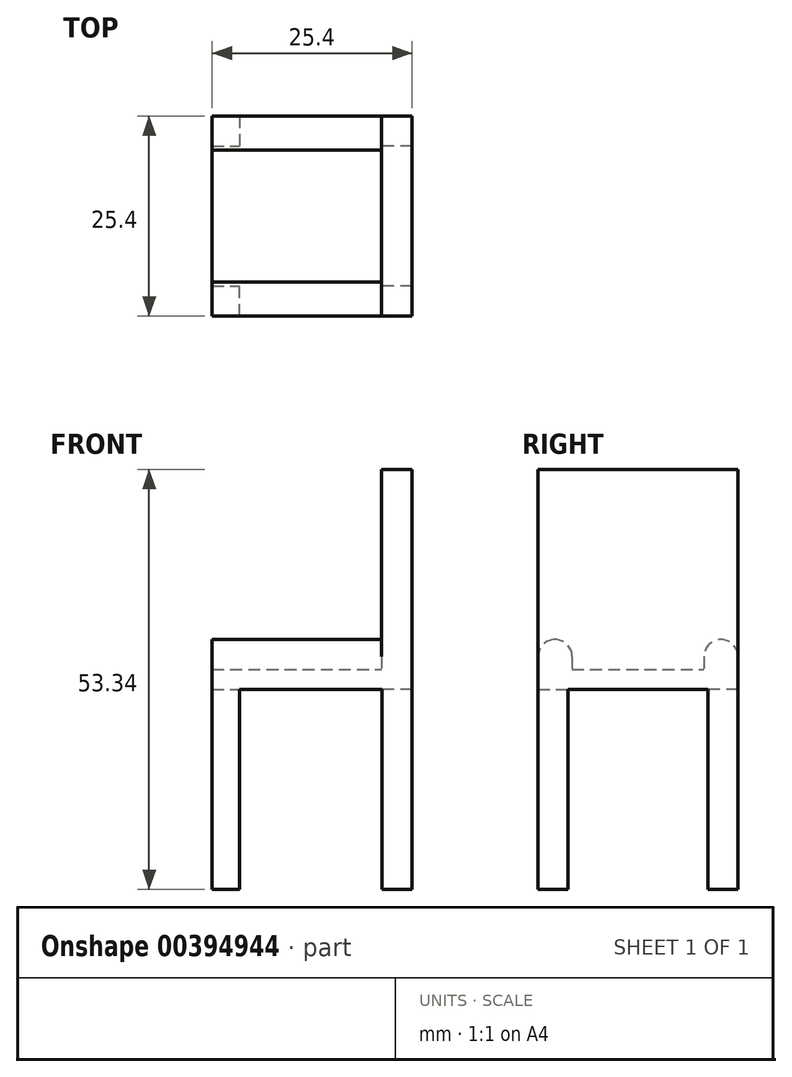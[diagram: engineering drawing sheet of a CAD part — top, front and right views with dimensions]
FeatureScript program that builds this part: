
annotation { "Feature Type Name" : "Feature", "Feature Type Description" : "" }
export const myFeature = defineFeature(function(context is Context, id is Id, definition is map)
    precondition{}
    {
        {
            var Q0;
            Q0=qCreatedBy(makeId("Top.planeOp"),FACE);
            var sketch = newSketch(context, id + "F0", { "sketchPlane" : qUnion([Q0])});
            skLineSegment(sketch, "E0.bottom", {"start": v(0, 0) * mm, "end": v(25.4, 0) * mm});
            skLineSegment(sketch, "E0.top", {"start": v(0, 25.4) * mm, "end": v(25.4, 25.4) * mm});
            skLineSegment(sketch, "E0.left", {"start": v(0, 0) * mm, "end": v(0, 25.4) * mm});
            skLineSegment(sketch, "E0.right", {"start": v(25.4, 0) * mm, "end": v(25.4, 25.4) * mm});
            skSolve(sketch);
        }
        {
            var Q0;
            Q0=makeQuery(id+"F0.imprint","IMPRINT",FACE,{"disambiguationData":[TD([[makeQuery(id+"F0.imprint","IMPRINT",EDGE,{"derivedFrom":sQuery(id+"F0.wireOp",EDGE,"E0.bottom")}),1.0]])]});
            extrude(context, id + "F1", {"entities" : qUnion([Q0]), "depth" : 2.54 * mm});
        }
        {
            var Q0;
            Q0=makeQuery(id+"F1.opExtrude","CAP_FACE",FACE,{"disambiguationData":[OSD([sQuery(id+"F0.wireOp",EDGE,"E0.bottom"),sQuery(id+"F0.wireOp",EDGE,"E0.top"),sQuery(id+"F0.wireOp",EDGE,"E0.left"),sQuery(id+"F0.wireOp",EDGE,"E0.right")])],"isStart":true});
            var sketch = newSketch(context, id + "F2", { "sketchPlane" : qUnion([Q0])});
            skLineSegment(sketch, "E1.bottom", {"start": v(0, 0) * mm, "end": v(3.47, 0) * mm});
            skLineSegment(sketch, "E1.top", {"start": v(0, -3.81) * mm, "end": v(3.47, -3.81) * mm});
            skLineSegment(sketch, "E1.left", {"start": v(0, 0) * mm, "end": v(0, -3.81) * mm});
            skLineSegment(sketch, "E1.right", {"start": v(3.47, 0) * mm, "end": v(3.47, -3.81) * mm});
            skLineSegment(sketch, "E2.bottom", {"start": v(25.4, 0) * mm, "end": v(21.6, 0) * mm});
            skLineSegment(sketch, "E2.top", {"start": v(25.4, -3.8) * mm, "end": v(21.6, -3.81) * mm});
            skLineSegment(sketch, "E2.left", {"start": v(25.4, 0) * mm, "end": v(25.4, -3.8) * mm});
            skLineSegment(sketch, "E2.right", {"start": v(21.6, 0) * mm, "end": v(21.6, -3.81) * mm});
            skLineSegment(sketch, "E3.bottom", {"start": v(0, -25.4) * mm, "end": v(3.47, -25.4) * mm});
            skLineSegment(sketch, "E3.top", {"start": v(0, -21.59) * mm, "end": v(3.47, -21.59) * mm});
            skLineSegment(sketch, "E3.left", {"start": v(0, -25.4) * mm, "end": v(0, -21.59) * mm});
            skLineSegment(sketch, "E3.right", {"start": v(3.47, -25.4) * mm, "end": v(3.47, -21.59) * mm});
            skLineSegment(sketch, "E4.bottom", {"start": v(25.4, -25.4) * mm, "end": v(21.6, -25.4) * mm});
            skLineSegment(sketch, "E4.top", {"start": v(25.4, -21.59) * mm, "end": v(21.6, -21.59) * mm});
            skLineSegment(sketch, "E4.left", {"start": v(25.4, -25.4) * mm, "end": v(25.4, -21.59) * mm});
            skLineSegment(sketch, "E4.right", {"start": v(21.6, -25.4) * mm, "end": v(21.6, -21.59) * mm});
            skSolve(sketch);
        }
        {
            var Q0;
            Q0 = qSketchRegion(id + "F2", true);
            extrude(context, id + "F3", {"entities" : qUnion([Q0]), "operationType" : NewBodyOperationType.ADD, "depth" : 25.4 * mm});
        }
        {
            var Q0;
            Q0=makeQuery(id+"F1.opExtrude","CAP_FACE",FACE,{"disambiguationData":[OSD([sQuery(id+"F0.wireOp",EDGE,"E0.bottom"),sQuery(id+"F0.wireOp",EDGE,"E0.top"),sQuery(id+"F0.wireOp",EDGE,"E0.left"),sQuery(id+"F0.wireOp",EDGE,"E0.right")])],"isStart":false});
            var sketch = newSketch(context, id + "F4", { "sketchPlane" : qUnion([Q0])});
            skLineSegment(sketch, "E5.bottom", {"start": v(21.54, 0) * mm, "end": v(25.4, 0) * mm});
            skLineSegment(sketch, "E5.top", {"start": v(21.54, 25.4) * mm, "end": v(25.4, 25.4) * mm});
            skLineSegment(sketch, "E5.left", {"start": v(21.54, 0) * mm, "end": v(21.54, 25.4) * mm});
            skLineSegment(sketch, "E5.right", {"start": v(25.4, 0) * mm, "end": v(25.4, 25.4) * mm});
            skSolve(sketch);
        }
        {
            var Q0;
            Q0=makeQuery(id+"F4.imprint","IMPRINT",FACE,{"disambiguationData":[TD([[makeQuery(id+"F4.imprint","IMPRINT",EDGE,{"derivedFrom":sQuery(id+"F4.wireOp",EDGE,"E5.bottom")}),1.0]])]});
            extrude(context, id + "F5", {"entities" : qUnion([Q0]), "operationType" : NewBodyOperationType.ADD, "depth" : 25.4 * mm});
        }
        {
            var Q0;
            Q0=makeQuery(id+"F1.opExtrude","CAP_FACE",FACE,{"disambiguationData":[OSD([sQuery(id+"F0.wireOp",EDGE,"E0.bottom"),sQuery(id+"F0.wireOp",EDGE,"E0.top"),sQuery(id+"F0.wireOp",EDGE,"E0.left"),sQuery(id+"F0.wireOp",EDGE,"E0.right")])],"isStart":false});
            var sketch = newSketch(context, id + "F6", { "sketchPlane" : qUnion([Q0])});
            skLineSegment(sketch, "E6.bottom", {"start": v(0, 21.08) * mm, "end": v(21.54, 21.08) * mm});
            skLineSegment(sketch, "E6.top", {"start": v(0, 25.4) * mm, "end": v(21.54, 25.4) * mm});
            skLineSegment(sketch, "E6.left", {"start": v(0, 21.08) * mm, "end": v(0, 25.4) * mm});
            skLineSegment(sketch, "E6.right", {"start": v(21.54, 21.08) * mm, "end": v(21.54, 25.4) * mm});
            skSolve(sketch);
        }
        {
            var Q0;
            Q0=makeQuery(id+"F6.imprint","IMPRINT",FACE,{"disambiguationData":[TD([[makeQuery(id+"F6.imprint","IMPRINT",EDGE,{"derivedFrom":sQuery(id+"F6.wireOp",EDGE,"E6.bottom")}),1.0]])]});
            extrude(context, id + "F7", {"entities" : qUnion([Q0]), "operationType" : NewBodyOperationType.ADD, "depth" : 3.8 * mm});
        }
        {
            var Q0;
            Q0=makeQuery(id+"F7.opExtrude","CAP_EDGE",EDGE,{"disambiguationData":[OSD([sQuery(id+"F6.wireOp",EDGE,"E6.top")])],"isStart":false});
            var Q1;
            Q1=makeQuery(id+"F7.opExtrude","CAP_EDGE",EDGE,{"disambiguationData":[OSD([sQuery(id+"F6.wireOp",EDGE,"E6.bottom")])],"isStart":false});
            fillet(context, id + "F8", {"entities" : qUnion([Q0, Q1]), "radius" : 2.16 * mm, "tangentPropagation" : true, "allowEdgeOverflow" : false});
        }
        {
            var Q0;
            Q0=makeQuery(id+"F1.opExtrude","CAP_FACE",FACE,{"disambiguationData":[OSD([sQuery(id+"F0.wireOp",EDGE,"E0.bottom"),sQuery(id+"F0.wireOp",EDGE,"E0.top"),sQuery(id+"F0.wireOp",EDGE,"E0.left"),sQuery(id+"F0.wireOp",EDGE,"E0.right")])],"isStart":false});
            var sketch = newSketch(context, id + "F9", { "sketchPlane" : qUnion([Q0])});
            skLineSegment(sketch, "E7.bottom", {"start": v(0, 4.32) * mm, "end": v(21.54, 4.32) * mm});
            skLineSegment(sketch, "E7.top", {"start": v(0, 0) * mm, "end": v(21.54, 0) * mm});
            skLineSegment(sketch, "E7.left", {"start": v(0, 4.32) * mm, "end": v(0, 0) * mm});
            skLineSegment(sketch, "E7.right", {"start": v(21.54, 4.32) * mm, "end": v(21.54, 0) * mm});
            skSolve(sketch);
        }
        {
            var Q0;
            Q0=makeQuery(id+"F9.imprint","IMPRINT",FACE,{"disambiguationData":[TD([[makeQuery(id+"F9.imprint","IMPRINT",EDGE,{"derivedFrom":sQuery(id+"F9.wireOp",EDGE,"E7.bottom")}),-1.0]])]});
            extrude(context, id + "F10", {"entities" : qUnion([Q0]), "operationType" : NewBodyOperationType.ADD, "depth" : 3.8 * mm});
        }
        {
            var Q0;
            Q0=makeQuery(id+"F10.opExtrude","CAP_EDGE",EDGE,{"disambiguationData":[OSD([sQuery(id+"F9.wireOp",EDGE,"E7.top")])],"isStart":false});
            fillet(context, id + "F11", {"entities" : qUnion([Q0]), "radius" : 2.16 * mm, "tangentPropagation" : true, "allowEdgeOverflow" : false});
        }
        {
            var Q0;
            Q0=makeQuery(id+"F10.opExtrude","CAP_EDGE",EDGE,{"disambiguationData":[OSD([sQuery(id+"F9.wireOp",EDGE,"E7.bottom")])],"isStart":false});
            fillet(context, id + "F12", {"entities" : qUnion([Q0]), "radius" : 2.16 * mm, "tangentPropagation" : true, "allowEdgeOverflow" : false});
        }
    });
